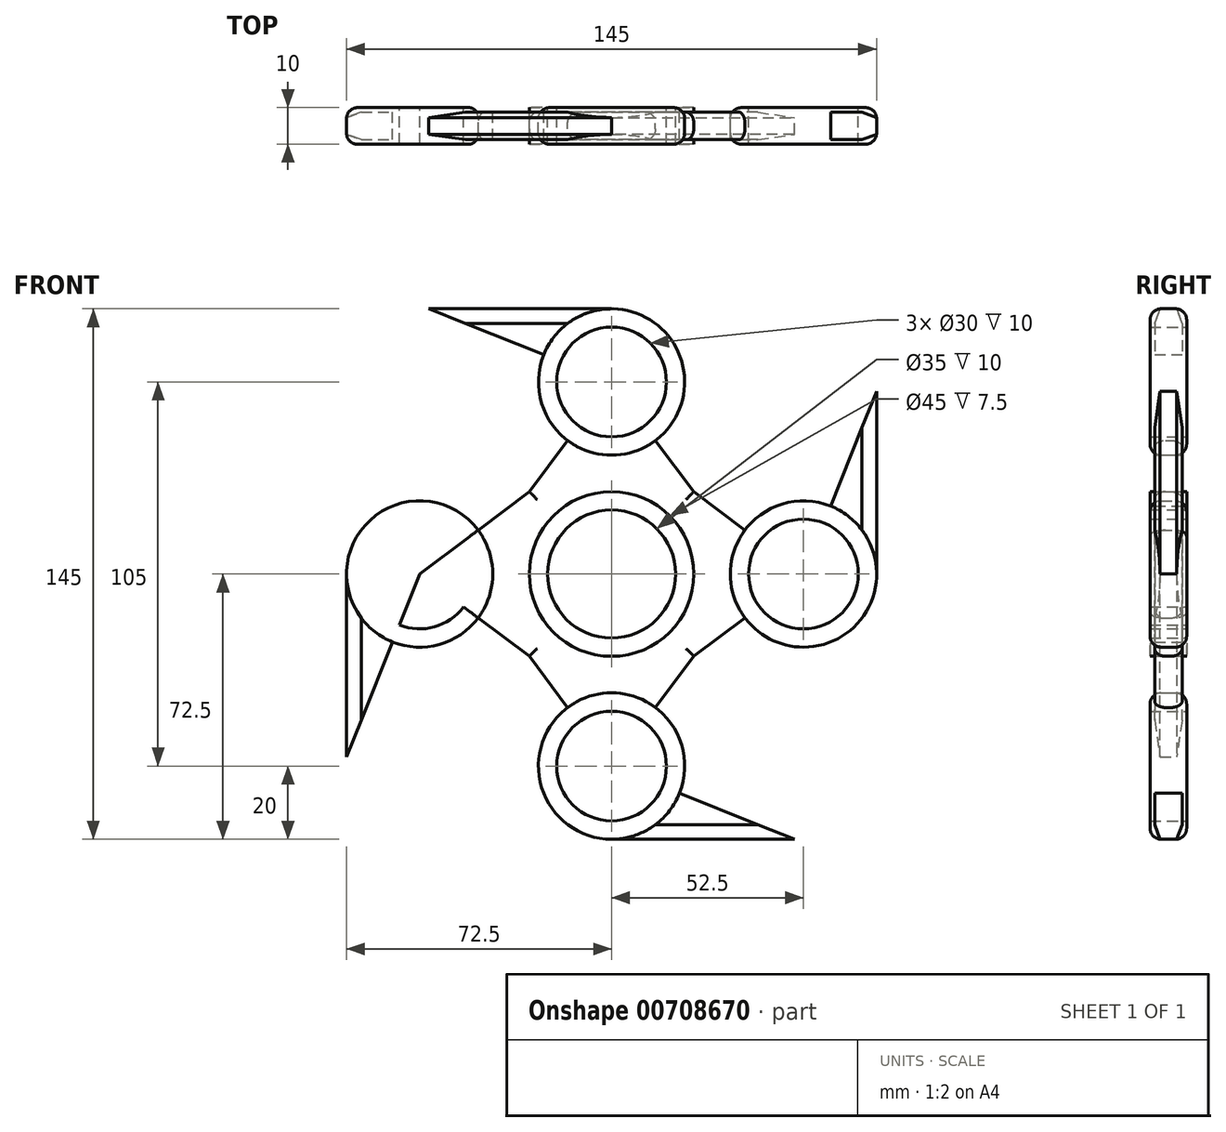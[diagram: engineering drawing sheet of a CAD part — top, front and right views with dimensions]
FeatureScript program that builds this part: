
annotation { "Feature Type Name" : "Feature", "Feature Type Description" : "" }
export const myFeature = defineFeature(function(context is Context, id is Id, definition is map)
    precondition{}
    {
        {
            var Q0;
            Q0=qCreatedBy(makeId("Front.planeOp"),FACE);
            var sketch = newSketch(context, id + "F0", { "sketchPlane" : qUnion([Q0])});
            skCircle(sketch, "E0", {"center": v(0, 0) * mm, "radius": 22.5 * mm});
            skLineSegment(sketch, "E1", {"start": v(0, 75.18) * mm, "end": v(0, -75.66) * mm});
            skLineSegment(sketch, "E2", {"start": v(-75.18, 0) * mm, "end": v(75.18, 0) * mm});
            skLineSegment(sketch, "E3.bottom", {"start": v(22.5, -22.5) * mm, "end": v(-22.5, -22.5) * mm});
            skLineSegment(sketch, "E3.top", {"start": v(22.5, 22.5) * mm, "end": v(-22.5, 22.5) * mm});
            skLineSegment(sketch, "E3.left", {"start": v(22.5, -22.5) * mm, "end": v(22.5, 22.5) * mm});
            skLineSegment(sketch, "E3.right", {"start": v(-22.5, -22.5) * mm, "end": v(-22.5, 22.5) * mm});
            skPoint(sketch, "E4", {"position": v(0, 52.5) * mm});
            skPoint(sketch, "E5", {"position": v(52.5, 0) * mm});
            skPoint(sketch, "E6", {"position": v(0, -52.5) * mm});
            skPoint(sketch, "E7", {"position": v(-52.5, 0) * mm});
            skCircle(sketch, "E8", {"center": v(-52.5, 0) * mm, "radius": 20 * mm});
            skCircle(sketch, "E9", {"center": v(0, 52.5) * mm, "radius": 20 * mm});
            skCircle(sketch, "E10", {"center": v(52.5, 0) * mm, "radius": 20 * mm});
            skCircle(sketch, "E11", {"center": v(0, -52.5) * mm, "radius": 20 * mm});
            skLineSegment(sketch, "E12", {"start": v(-22.5, 22.5) * mm, "end": v(0, 52.5) * mm});
            skLineSegment(sketch, "E13", {"start": v(22.5, 22.5) * mm, "end": v(0, 52.5) * mm});
            skLineSegment(sketch, "E14", {"start": v(22.5, 22.5) * mm, "end": v(52.5, 0) * mm});
            skLineSegment(sketch, "E15", {"start": v(22.5, -22.5) * mm, "end": v(52.5, 0) * mm});
            skLineSegment(sketch, "E16", {"start": v(22.5, -22.5) * mm, "end": v(0, -52.5) * mm});
            skLineSegment(sketch, "E17", {"start": v(-22.5, -22.5) * mm, "end": v(0, -52.5) * mm});
            skLineSegment(sketch, "E18", {"start": v(-22.5, -22.5) * mm, "end": v(-52.5, 0) * mm});
            skLineSegment(sketch, "E19", {"start": v(-52.5, 0) * mm, "end": v(-22.5, 22.5) * mm});
            skPoint(sketch, "E20", {"position": v(0, 72.5) * mm});
            skPoint(sketch, "E21", {"position": v(72.5, 0) * mm});
            skPoint(sketch, "E22", {"position": v(0, -72.5) * mm});
            skPoint(sketch, "E23", {"position": v(-72.5, 0) * mm});
            skLineSegment(sketch, "E24", {"start": v(0, 72.5) * mm, "end": v(-50, 72.5) * mm});
            skLineSegment(sketch, "E25", {"start": v(-50, 72.5) * mm, "end": v(0, 52.5) * mm});
            skLineSegment(sketch, "E26", {"start": v(72.5, 0) * mm, "end": v(72.5, 50) * mm});
            skLineSegment(sketch, "E27", {"start": v(72.5, 50) * mm, "end": v(52.5, 0) * mm});
            skLineSegment(sketch, "E28", {"start": v(0, -72.5) * mm, "end": v(50, -72.5) * mm});
            skLineSegment(sketch, "E29", {"start": v(50, -72.5) * mm, "end": v(0, -52.5) * mm});
            skLineSegment(sketch, "E30", {"start": v(-72.5, 0) * mm, "end": v(-72.5, -50) * mm});
            skLineSegment(sketch, "E31", {"start": v(-72.5, -50) * mm, "end": v(-52.5, 0) * mm});
            skCircle(sketch, "E32", {"center": v(0, 52.5) * mm, "radius": 15 * mm});
            skCircle(sketch, "E33", {"center": v(-52.5, 0) * mm, "radius": 15 * mm});
            skCircle(sketch, "E34", {"center": v(52.5, 0) * mm, "radius": 15 * mm});
            skCircle(sketch, "E35", {"center": v(0, -52.5) * mm, "radius": 15 * mm});
            skCircle(sketch, "E36", {"center": v(0, 0) * mm, "radius": 17.5 * mm});
            skSolve(sketch);
        }
        {
            var Q0;
            {var subQ0=sQuery(id+"F0.wireOp",EDGE,"E24");Q0=makeQuery(id+"F0.imprint","IMPRINT",FACE,{"disambiguationData":[TD([[makeQuery(id+"F0.imprint","IMPRINT",EDGE,{"derivedFrom":subQ0}),1.0]])]});}
            var Q1;
            {var subQ0=sQuery(id+"F0.wireOp",EDGE,"E26");Q1=makeQuery(id+"F0.imprint","IMPRINT",FACE,{"disambiguationData":[TD([[makeQuery(id+"F0.imprint","IMPRINT",EDGE,{"derivedFrom":subQ0}),1.0]])]});}
            var Q2;
            {var subQ0=sQuery(id+"F0.wireOp",EDGE,"E28");Q2=makeQuery(id+"F0.imprint","IMPRINT",FACE,{"disambiguationData":[TD([[makeQuery(id+"F0.imprint","IMPRINT",EDGE,{"derivedFrom":subQ0}),1.0]])]});}
            var Q3;
            {var subQ0=sQuery(id+"F0.wireOp",EDGE,"E30");Q3=makeQuery(id+"F0.imprint","IMPRINT",FACE,{"disambiguationData":[TD([[makeQuery(id+"F0.imprint","IMPRINT",EDGE,{"derivedFrom":subQ0}),1.0]])]});}
            var Q4;
            {var subQ0=sQuery(id+"F0.wireOp",EDGE,"E8");var subQ5=sQuery(id+"F0.wireOp",EDGE,"E18");var subQ6=makeQuery(id+"F0.imprint","INTERSECT",VERTEX,{"derivedFrom":[subQ0,subQ5]});Q4=makeQuery(id+"F0.imprint","IMPRINT",FACE,{"disambiguationData":[TD([[makeQuery(id+"F0.imprint","IMPRINT",EDGE,{"disambiguationData":[TD([[subQ6,-1.0]])],"derivedFrom":subQ0}),-1.0]])]});}
            var Q5;
            {var subQ0=sQuery(id+"F0.wireOp",EDGE,"E8");var subQ5=sQuery(id+"F0.wireOp",EDGE,"E19");var subQ7=makeQuery(id+"F0.imprint","INTERSECT",VERTEX,{"derivedFrom":[subQ0,subQ5]});Q5=makeQuery(id+"F0.imprint","IMPRINT",FACE,{"disambiguationData":[TD([[makeQuery(id+"F0.imprint","IMPRINT",EDGE,{"disambiguationData":[TD([[subQ7,1.0]])],"derivedFrom":subQ0}),-1.0]])]});}
            var Q6;
            {var subQ0=sQuery(id+"F0.wireOp",EDGE,"E9");var subQ5=sQuery(id+"F0.wireOp",EDGE,"E12");var subQ6=makeQuery(id+"F0.imprint","INTERSECT",VERTEX,{"derivedFrom":[subQ0,subQ5]});Q6=makeQuery(id+"F0.imprint","IMPRINT",FACE,{"disambiguationData":[TD([[makeQuery(id+"F0.imprint","IMPRINT",EDGE,{"disambiguationData":[TD([[subQ6,-1.0]])],"derivedFrom":subQ0}),-1.0]])]});}
            var Q7;
            {var subQ0=sQuery(id+"F0.wireOp",EDGE,"E9");var subQ5=sQuery(id+"F0.wireOp",EDGE,"E13");var subQ7=makeQuery(id+"F0.imprint","INTERSECT",VERTEX,{"derivedFrom":[subQ0,subQ5]});Q7=makeQuery(id+"F0.imprint","IMPRINT",FACE,{"disambiguationData":[TD([[makeQuery(id+"F0.imprint","IMPRINT",EDGE,{"disambiguationData":[TD([[subQ7,1.0]])],"derivedFrom":subQ0}),-1.0]])]});}
            var Q8;
            {var subQ0=sQuery(id+"F0.wireOp",EDGE,"E10");var subQ5=sQuery(id+"F0.wireOp",EDGE,"E14");var subQ7=makeQuery(id+"F0.imprint","INTERSECT",VERTEX,{"derivedFrom":[subQ0,subQ5]});Q8=makeQuery(id+"F0.imprint","IMPRINT",FACE,{"disambiguationData":[TD([[makeQuery(id+"F0.imprint","IMPRINT",EDGE,{"disambiguationData":[TD([[subQ7,-1.0]])],"derivedFrom":subQ0}),-1.0]])]});}
            var Q9;
            {var subQ0=sQuery(id+"F0.wireOp",EDGE,"E10");var subQ5=sQuery(id+"F0.wireOp",EDGE,"E15");var subQ7=makeQuery(id+"F0.imprint","INTERSECT",VERTEX,{"derivedFrom":[subQ0,subQ5]});Q9=makeQuery(id+"F0.imprint","IMPRINT",FACE,{"disambiguationData":[TD([[makeQuery(id+"F0.imprint","IMPRINT",EDGE,{"disambiguationData":[TD([[subQ7,1.0]])],"derivedFrom":subQ0}),-1.0]])]});}
            var Q10;
            {var subQ0=sQuery(id+"F0.wireOp",EDGE,"E11");var subQ5=sQuery(id+"F0.wireOp",EDGE,"E16");var subQ6=makeQuery(id+"F0.imprint","INTERSECT",VERTEX,{"derivedFrom":[subQ0,subQ5]});Q10=makeQuery(id+"F0.imprint","IMPRINT",FACE,{"disambiguationData":[TD([[makeQuery(id+"F0.imprint","IMPRINT",EDGE,{"disambiguationData":[TD([[subQ6,-1.0]])],"derivedFrom":subQ0}),-1.0]])]});}
            var Q11;
            {var subQ0=sQuery(id+"F0.wireOp",EDGE,"E11");var subQ5=sQuery(id+"F0.wireOp",EDGE,"E17");var subQ7=makeQuery(id+"F0.imprint","INTERSECT",VERTEX,{"derivedFrom":[subQ0,subQ5]});Q11=makeQuery(id+"F0.imprint","IMPRINT",FACE,{"disambiguationData":[TD([[makeQuery(id+"F0.imprint","IMPRINT",EDGE,{"disambiguationData":[TD([[subQ7,1.0]])],"derivedFrom":subQ0}),-1.0]])]});}
            var Q12;
            {var subQ0=sQuery(id+"F0.wireOp",EDGE,"E3.right");var subQ1=sQuery(id+"F0.wireOp",EDGE,"E0");var subQ2=makeQuery(id+"F0.imprint","INTERSECT",VERTEX,{"derivedFrom":[subQ1,sQuery(id+"F0.wireOp",EDGE,"E2"),subQ0]});Q12=makeQuery(id+"F0.imprint","IMPRINT",FACE,{"disambiguationData":[TD([[makeQuery(id+"F0.imprint","IMPRINT",EDGE,{"disambiguationData":[TD([[subQ2,-1.0]])],"derivedFrom":subQ1}),-1.0]])]});}
            var Q13;
            {var subQ0=sQuery(id+"F0.wireOp",EDGE,"E3.top");var subQ1=sQuery(id+"F0.wireOp",EDGE,"E0");var subQ2=makeQuery(id+"F0.imprint","INTERSECT",VERTEX,{"derivedFrom":[subQ1,sQuery(id+"F0.wireOp",EDGE,"E1"),subQ0]});Q13=makeQuery(id+"F0.imprint","IMPRINT",FACE,{"disambiguationData":[TD([[makeQuery(id+"F0.imprint","IMPRINT",EDGE,{"disambiguationData":[TD([[subQ2,-1.0]])],"derivedFrom":subQ1}),-1.0]])]});}
            var Q14;
            {var subQ0=sQuery(id+"F0.wireOp",EDGE,"E3.top");var subQ1=sQuery(id+"F0.wireOp",EDGE,"E0");var subQ2=makeQuery(id+"F0.imprint","INTERSECT",VERTEX,{"derivedFrom":[subQ1,sQuery(id+"F0.wireOp",EDGE,"E1"),subQ0]});Q14=makeQuery(id+"F0.imprint","IMPRINT",FACE,{"disambiguationData":[TD([[makeQuery(id+"F0.imprint","IMPRINT",EDGE,{"disambiguationData":[TD([[subQ2,1.0]])],"derivedFrom":subQ1}),-1.0]])]});}
            var Q15;
            {var subQ0=sQuery(id+"F0.wireOp",EDGE,"E3.left");var subQ1=sQuery(id+"F0.wireOp",EDGE,"E0");var subQ2=makeQuery(id+"F0.imprint","INTERSECT",VERTEX,{"derivedFrom":[subQ1,sQuery(id+"F0.wireOp",EDGE,"E2"),subQ0]});Q15=makeQuery(id+"F0.imprint","IMPRINT",FACE,{"disambiguationData":[TD([[makeQuery(id+"F0.imprint","IMPRINT",EDGE,{"disambiguationData":[TD([[subQ2,1.0]])],"derivedFrom":subQ1}),-1.0]])]});}
            extrude(context, id + "F1", {"entities" : qUnion([Q0, Q1, Q2, Q3, Q4, Q5, Q6, Q7, Q8, Q9, Q10, Q11, Q12, Q13, Q14, Q15]), "endBound" : BoundingType.SYMMETRIC, "depth" : 7.5 * mm, "offsetDistance" : 25 * mm});
        }
        {
            var Q0;
            {var subQ0=sQuery(id+"F0.wireOp",EDGE,"E8");var subQ5=sQuery(id+"F0.wireOp",EDGE,"E19");var subQ6=makeQuery(id+"F0.imprint","INTERSECT",VERTEX,{"derivedFrom":[subQ0,subQ5]});Q0=makeQuery(id+"F0.imprint","IMPRINT",FACE,{"disambiguationData":[TD([[makeQuery(id+"F0.imprint","IMPRINT",EDGE,{"disambiguationData":[TD([[subQ6,1.0]])],"derivedFrom":subQ5}),1.0]])]});}
            var Q1;
            {var subQ0=sQuery(id+"F0.wireOp",EDGE,"E8");var subQ5=sQuery(id+"F0.wireOp",EDGE,"E31");var subQ6=makeQuery(id+"F0.imprint","INTERSECT",VERTEX,{"derivedFrom":[subQ0,subQ5]});Q1=makeQuery(id+"F0.imprint","IMPRINT",FACE,{"disambiguationData":[TD([[makeQuery(id+"F0.imprint","IMPRINT",EDGE,{"disambiguationData":[TD([[subQ6,-1.0]])],"derivedFrom":subQ5}),1.0]])]});}
            var Q2;
            {var subQ0=sQuery(id+"F0.wireOp",EDGE,"E31");var subQ1=sQuery(id+"F0.wireOp",EDGE,"E8");var subQ2=makeQuery(id+"F0.imprint","INTERSECT",VERTEX,{"derivedFrom":[subQ1,subQ0]});Q2=makeQuery(id+"F0.imprint","IMPRINT",FACE,{"disambiguationData":[TD([[makeQuery(id+"F0.imprint","IMPRINT",EDGE,{"disambiguationData":[TD([[subQ2,-1.0]])],"derivedFrom":subQ1}),1.0]])]});}
            var Q3;
            {var subQ0=sQuery(id+"F0.wireOp",EDGE,"E33");var subQ1=sQuery(id+"F0.wireOp",EDGE,"E2");var subQ2=makeQuery(id+"F0.imprint","INTERSECT",VERTEX,{"disambiguationData":[OD(1.0)],"derivedFrom":[subQ1,subQ0]});Q3=makeQuery(id+"F0.imprint","IMPRINT",FACE,{"disambiguationData":[TD([[makeQuery(id+"F0.imprint","IMPRINT",EDGE,{"disambiguationData":[TD([[subQ2,-1.0]])],"derivedFrom":subQ1}),-1.0]])]});}
            var Q4;
            {var subQ0=sQuery(id+"F0.wireOp",EDGE,"E33");var subQ1=sQuery(id+"F0.wireOp",EDGE,"E2");var subQ2=makeQuery(id+"F0.imprint","INTERSECT",VERTEX,{"disambiguationData":[OD(1.0)],"derivedFrom":[subQ1,subQ0]});Q4=makeQuery(id+"F0.imprint","IMPRINT",FACE,{"disambiguationData":[TD([[makeQuery(id+"F0.imprint","IMPRINT",EDGE,{"disambiguationData":[TD([[subQ2,-1.0]])],"derivedFrom":subQ1}),1.0]])]});}
            var Q5;
            {var subQ0=sQuery(id+"F0.wireOp",EDGE,"E25");var subQ1=sQuery(id+"F0.wireOp",EDGE,"E9");var subQ2=makeQuery(id+"F0.imprint","INTERSECT",VERTEX,{"derivedFrom":[subQ1,subQ0]});Q5=makeQuery(id+"F0.imprint","IMPRINT",FACE,{"disambiguationData":[TD([[makeQuery(id+"F0.imprint","IMPRINT",EDGE,{"disambiguationData":[TD([[subQ2,-1.0]])],"derivedFrom":subQ1}),1.0]])]});}
            var Q6;
            {var subQ0=sQuery(id+"F0.wireOp",EDGE,"E9");var subQ5=sQuery(id+"F0.wireOp",EDGE,"E25");var subQ6=makeQuery(id+"F0.imprint","INTERSECT",VERTEX,{"derivedFrom":[subQ0,subQ5]});Q6=makeQuery(id+"F0.imprint","IMPRINT",FACE,{"disambiguationData":[TD([[makeQuery(id+"F0.imprint","IMPRINT",EDGE,{"disambiguationData":[TD([[subQ6,-1.0]])],"derivedFrom":subQ5}),1.0]])]});}
            var Q7;
            {var subQ0=sQuery(id+"F0.wireOp",EDGE,"E9");var subQ5=sQuery(id+"F0.wireOp",EDGE,"E13");var subQ6=makeQuery(id+"F0.imprint","INTERSECT",VERTEX,{"derivedFrom":[subQ0,subQ5]});Q7=makeQuery(id+"F0.imprint","IMPRINT",FACE,{"disambiguationData":[TD([[makeQuery(id+"F0.imprint","IMPRINT",EDGE,{"disambiguationData":[TD([[subQ6,-1.0]])],"derivedFrom":subQ5}),-1.0]])]});}
            var Q8;
            {var subQ0=sQuery(id+"F0.wireOp",EDGE,"E32");var subQ1=sQuery(id+"F0.wireOp",EDGE,"E1");var subQ2=makeQuery(id+"F0.imprint","INTERSECT",VERTEX,{"disambiguationData":[OD(1.0)],"derivedFrom":[subQ1,subQ0]});Q8=makeQuery(id+"F0.imprint","IMPRINT",FACE,{"disambiguationData":[TD([[makeQuery(id+"F0.imprint","IMPRINT",EDGE,{"disambiguationData":[TD([[subQ2,-1.0]])],"derivedFrom":subQ1}),1.0]])]});}
            var Q9;
            {var subQ0=sQuery(id+"F0.wireOp",EDGE,"E32");var subQ1=sQuery(id+"F0.wireOp",EDGE,"E1");var subQ2=makeQuery(id+"F0.imprint","INTERSECT",VERTEX,{"disambiguationData":[OD(1.0)],"derivedFrom":[subQ1,subQ0]});Q9=makeQuery(id+"F0.imprint","IMPRINT",FACE,{"disambiguationData":[TD([[makeQuery(id+"F0.imprint","IMPRINT",EDGE,{"disambiguationData":[TD([[subQ2,-1.0]])],"derivedFrom":subQ1}),-1.0]])]});}
            var Q10;
            {var subQ0=sQuery(id+"F0.wireOp",EDGE,"E27");var subQ1=sQuery(id+"F0.wireOp",EDGE,"E10");var subQ2=makeQuery(id+"F0.imprint","INTERSECT",VERTEX,{"derivedFrom":[subQ1,subQ0]});Q10=makeQuery(id+"F0.imprint","IMPRINT",FACE,{"disambiguationData":[TD([[makeQuery(id+"F0.imprint","IMPRINT",EDGE,{"disambiguationData":[TD([[subQ2,-1.0]])],"derivedFrom":subQ1}),1.0]])]});}
            var Q11;
            {var subQ0=sQuery(id+"F0.wireOp",EDGE,"E10");var subQ5=sQuery(id+"F0.wireOp",EDGE,"E27");var subQ6=makeQuery(id+"F0.imprint","INTERSECT",VERTEX,{"derivedFrom":[subQ0,subQ5]});Q11=makeQuery(id+"F0.imprint","IMPRINT",FACE,{"disambiguationData":[TD([[makeQuery(id+"F0.imprint","IMPRINT",EDGE,{"disambiguationData":[TD([[subQ6,-1.0]])],"derivedFrom":subQ5}),1.0]])]});}
            var Q12;
            {var subQ0=sQuery(id+"F0.wireOp",EDGE,"E10");var subQ5=sQuery(id+"F0.wireOp",EDGE,"E15");var subQ6=makeQuery(id+"F0.imprint","INTERSECT",VERTEX,{"derivedFrom":[subQ0,subQ5]});Q12=makeQuery(id+"F0.imprint","IMPRINT",FACE,{"disambiguationData":[TD([[makeQuery(id+"F0.imprint","IMPRINT",EDGE,{"disambiguationData":[TD([[subQ6,-1.0]])],"derivedFrom":subQ5}),-1.0]])]});}
            var Q13;
            {var subQ0=sQuery(id+"F0.wireOp",EDGE,"E10");var subQ1=sQuery(id+"F0.wireOp",EDGE,"E2");var subQ2=makeQuery(id+"F0.imprint","INTERSECT",VERTEX,{"derivedFrom":[subQ1,subQ0]});Q13=makeQuery(id+"F0.imprint","IMPRINT",FACE,{"disambiguationData":[TD([[makeQuery(id+"F0.imprint","IMPRINT",EDGE,{"disambiguationData":[TD([[subQ2,-1.0]])],"derivedFrom":subQ1}),-1.0]])]});}
            var Q14;
            {var subQ0=sQuery(id+"F0.wireOp",EDGE,"E10");var subQ1=sQuery(id+"F0.wireOp",EDGE,"E2");var subQ2=makeQuery(id+"F0.imprint","INTERSECT",VERTEX,{"derivedFrom":[subQ1,subQ0]});Q14=makeQuery(id+"F0.imprint","IMPRINT",FACE,{"disambiguationData":[TD([[makeQuery(id+"F0.imprint","IMPRINT",EDGE,{"disambiguationData":[TD([[subQ2,-1.0]])],"derivedFrom":subQ1}),1.0]])]});}
            var Q15;
            {var subQ0=sQuery(id+"F0.wireOp",EDGE,"E11");var subQ1=sQuery(id+"F0.wireOp",EDGE,"E1");var subQ2=makeQuery(id+"F0.imprint","INTERSECT",VERTEX,{"derivedFrom":[subQ1,subQ0]});Q15=makeQuery(id+"F0.imprint","IMPRINT",FACE,{"disambiguationData":[TD([[makeQuery(id+"F0.imprint","IMPRINT",EDGE,{"disambiguationData":[TD([[subQ2,-1.0]])],"derivedFrom":subQ1}),1.0]])]});}
            var Q16;
            {var subQ0=sQuery(id+"F0.wireOp",EDGE,"E16");var subQ1=sQuery(id+"F0.wireOp",EDGE,"E11");var subQ2=makeQuery(id+"F0.imprint","INTERSECT",VERTEX,{"derivedFrom":[subQ1,subQ0]});Q16=makeQuery(id+"F0.imprint","IMPRINT",FACE,{"disambiguationData":[TD([[makeQuery(id+"F0.imprint","IMPRINT",EDGE,{"disambiguationData":[TD([[subQ2,1.0]])],"derivedFrom":subQ1}),1.0]])]});}
            var Q17;
            {var subQ0=sQuery(id+"F0.wireOp",EDGE,"E11");var subQ5=sQuery(id+"F0.wireOp",EDGE,"E29");var subQ6=makeQuery(id+"F0.imprint","INTERSECT",VERTEX,{"derivedFrom":[subQ0,subQ5]});Q17=makeQuery(id+"F0.imprint","IMPRINT",FACE,{"disambiguationData":[TD([[makeQuery(id+"F0.imprint","IMPRINT",EDGE,{"disambiguationData":[TD([[subQ6,-1.0]])],"derivedFrom":subQ5}),1.0]])]});}
            var Q18;
            {var subQ0=sQuery(id+"F0.wireOp",EDGE,"E11");var subQ5=sQuery(id+"F0.wireOp",EDGE,"E17");var subQ6=makeQuery(id+"F0.imprint","INTERSECT",VERTEX,{"derivedFrom":[subQ0,subQ5]});Q18=makeQuery(id+"F0.imprint","IMPRINT",FACE,{"disambiguationData":[TD([[makeQuery(id+"F0.imprint","IMPRINT",EDGE,{"disambiguationData":[TD([[subQ6,-1.0]])],"derivedFrom":subQ5}),-1.0]])]});}
            var Q19;
            {var subQ0=sQuery(id+"F0.wireOp",EDGE,"E11");var subQ1=sQuery(id+"F0.wireOp",EDGE,"E1");var subQ2=makeQuery(id+"F0.imprint","INTERSECT",VERTEX,{"derivedFrom":[subQ1,subQ0]});Q19=makeQuery(id+"F0.imprint","IMPRINT",FACE,{"disambiguationData":[TD([[makeQuery(id+"F0.imprint","IMPRINT",EDGE,{"disambiguationData":[TD([[subQ2,-1.0]])],"derivedFrom":subQ1}),-1.0]])]});}
            var Q20;
            {var subQ3=sQuery(id+"F0.wireOp",EDGE,"E1");var subQ5=sQuery(id+"F0.wireOp",EDGE,"E36");var subQ6=makeQuery(id+"F0.imprint","INTERSECT",VERTEX,{"disambiguationData":[OD(1.0)],"derivedFrom":[subQ3,subQ5]});Q20=makeQuery(id+"F0.imprint","IMPRINT",FACE,{"disambiguationData":[TD([[makeQuery(id+"F0.imprint","IMPRINT",EDGE,{"disambiguationData":[TD([[subQ6,1.0]])],"derivedFrom":subQ5}),-1.0]])]});}
            var Q21;
            {var subQ3=sQuery(id+"F0.wireOp",EDGE,"E1");var subQ5=sQuery(id+"F0.wireOp",EDGE,"E36");var subQ6=makeQuery(id+"F0.imprint","INTERSECT",VERTEX,{"disambiguationData":[OD(1.0)],"derivedFrom":[subQ3,subQ5]});Q21=makeQuery(id+"F0.imprint","IMPRINT",FACE,{"disambiguationData":[TD([[makeQuery(id+"F0.imprint","IMPRINT",EDGE,{"disambiguationData":[TD([[subQ6,-1.0]])],"derivedFrom":subQ5}),-1.0]])]});}
            var Q22;
            {var subQ0=sQuery(id+"F0.wireOp",EDGE,"E1");var subQ5=sQuery(id+"F0.wireOp",EDGE,"E36");var subQ6=makeQuery(id+"F0.imprint","INTERSECT",VERTEX,{"disambiguationData":[OD(0.0)],"derivedFrom":[subQ0,subQ5]});Q22=makeQuery(id+"F0.imprint","IMPRINT",FACE,{"disambiguationData":[TD([[makeQuery(id+"F0.imprint","IMPRINT",EDGE,{"disambiguationData":[TD([[subQ6,1.0]])],"derivedFrom":subQ5}),-1.0]])]});}
            var Q23;
            {var subQ0=sQuery(id+"F0.wireOp",EDGE,"E1");var subQ5=sQuery(id+"F0.wireOp",EDGE,"E36");var subQ6=makeQuery(id+"F0.imprint","INTERSECT",VERTEX,{"disambiguationData":[OD(0.0)],"derivedFrom":[subQ0,subQ5]});Q23=makeQuery(id+"F0.imprint","IMPRINT",FACE,{"disambiguationData":[TD([[makeQuery(id+"F0.imprint","IMPRINT",EDGE,{"disambiguationData":[TD([[subQ6,-1.0]])],"derivedFrom":subQ5}),-1.0]])]});}
            extrude(context, id + "F2", {"entities" : qUnion([Q0, Q1, Q2, Q3, Q4, Q5, Q6, Q7, Q8, Q9, Q10, Q11, Q12, Q13, Q14, Q15, Q16, Q17, Q18, Q19, Q20, Q21, Q22, Q23]), "endBound" : BoundingType.SYMMETRIC, "depth" : 10 * mm, "offsetDistance" : 25 * mm});
        }
        {
            var Q0;
            Q0=makeQuery(id+"F1.opExtrude","CAP_EDGE",EDGE,{"disambiguationData":[OSD([sQuery(id+"F0.wireOp",EDGE,"E24")])],"isStart":false});
            var Q1;
            Q1=makeQuery(id+"F1.opExtrude","CAP_EDGE",EDGE,{"disambiguationData":[OSD([sQuery(id+"F0.wireOp",EDGE,"E26")])],"isStart":false});
            var Q2;
            Q2=makeQuery(id+"F1.opExtrude","CAP_EDGE",EDGE,{"disambiguationData":[OSD([sQuery(id+"F0.wireOp",EDGE,"E28")])],"isStart":false});
            var Q3;
            Q3=makeQuery(id+"F1.opExtrude","CAP_EDGE",EDGE,{"disambiguationData":[OSD([sQuery(id+"F0.wireOp",EDGE,"E30")])],"isStart":false});
            chamfer(context, id + "F3", {"entities" : qUnion([Q0, Q1, Q2, Q3]), "chamferType" : ChamferType.OFFSET_ANGLE, "width" : 4 * mm, "oppositeDirection" : false, "angle" : 20 * degree, "tangentPropagation" : true});
        }
        {
            var Q0;
            Q0=makeQuery(id+"F1.opExtrude","CAP_EDGE",EDGE,{"disambiguationData":[OSD([sQuery(id+"F0.wireOp",EDGE,"E30")])],"isStart":true});
            var Q1;
            Q1=makeQuery(id+"F1.opExtrude","CAP_EDGE",EDGE,{"disambiguationData":[OSD([sQuery(id+"F0.wireOp",EDGE,"E28")])],"isStart":true});
            var Q2;
            Q2=makeQuery(id+"F1.opExtrude","CAP_EDGE",EDGE,{"disambiguationData":[OSD([sQuery(id+"F0.wireOp",EDGE,"E26")])],"isStart":true});
            var Q3;
            Q3=makeQuery(id+"F1.opExtrude","CAP_EDGE",EDGE,{"disambiguationData":[OSD([sQuery(id+"F0.wireOp",EDGE,"E24")])],"isStart":true});
            chamfer(context, id + "F4", {"entities" : qUnion([Q0, Q1, Q2, Q3]), "chamferType" : ChamferType.OFFSET_ANGLE, "width" : 4 * mm, "oppositeDirection" : true, "angle" : 20 * degree, "tangentPropagation" : true});
        }
        {
            var Q0;
            Q0=makeQuery(id+"F1.opExtrude","CAP_EDGE",EDGE,{"disambiguationData":[OSD([sQuery(id+"F0.wireOp",EDGE,"E12")])],"isStart":false});
            var Q1;
            Q1=makeQuery(id+"F1.opExtrude","CAP_EDGE",EDGE,{"disambiguationData":[OSD([sQuery(id+"F0.wireOp",EDGE,"E19")])],"isStart":false});
            var Q2;
            Q2=makeQuery(id+"F1.opExtrude","CAP_EDGE",EDGE,{"disambiguationData":[OSD([sQuery(id+"F0.wireOp",EDGE,"E13")])],"isStart":false});
            var Q3;
            Q3=makeQuery(id+"F1.opExtrude","CAP_EDGE",EDGE,{"disambiguationData":[OSD([sQuery(id+"F0.wireOp",EDGE,"E14")])],"isStart":false});
            var Q4;
            Q4=makeQuery(id+"F1.opExtrude","CAP_EDGE",EDGE,{"disambiguationData":[OSD([sQuery(id+"F0.wireOp",EDGE,"E15")])],"isStart":false});
            var Q5;
            Q5=makeQuery(id+"F1.opExtrude","CAP_EDGE",EDGE,{"disambiguationData":[OSD([sQuery(id+"F0.wireOp",EDGE,"E16")])],"isStart":false});
            var Q6;
            Q6=makeQuery(id+"F1.opExtrude","CAP_EDGE",EDGE,{"disambiguationData":[OSD([sQuery(id+"F0.wireOp",EDGE,"E18")])],"isStart":false});
            var Q7;
            Q7=makeQuery(id+"F1.opExtrude","CAP_EDGE",EDGE,{"disambiguationData":[OSD([sQuery(id+"F0.wireOp",EDGE,"E17")])],"isStart":false});
            var Q8;
            Q8=makeQuery(id+"F1.opExtrude","CAP_EDGE",EDGE,{"disambiguationData":[OSD([sQuery(id+"F0.wireOp",EDGE,"E18")])],"isStart":true});
            var Q9;
            Q9=makeQuery(id+"F1.opExtrude","CAP_EDGE",EDGE,{"disambiguationData":[OSD([sQuery(id+"F0.wireOp",EDGE,"E17")])],"isStart":true});
            var Q10;
            Q10=makeQuery(id+"F1.opExtrude","CAP_EDGE",EDGE,{"disambiguationData":[OSD([sQuery(id+"F0.wireOp",EDGE,"E16")])],"isStart":true});
            var Q11;
            Q11=makeQuery(id+"F1.opExtrude","CAP_EDGE",EDGE,{"disambiguationData":[OSD([sQuery(id+"F0.wireOp",EDGE,"E15")])],"isStart":true});
            var Q12;
            Q12=makeQuery(id+"F1.opExtrude","CAP_EDGE",EDGE,{"disambiguationData":[OSD([sQuery(id+"F0.wireOp",EDGE,"E14")])],"isStart":true});
            var Q13;
            Q13=makeQuery(id+"F1.opExtrude","CAP_EDGE",EDGE,{"disambiguationData":[OSD([sQuery(id+"F0.wireOp",EDGE,"E13")])],"isStart":true});
            var Q14;
            Q14=makeQuery(id+"F1.opExtrude","CAP_EDGE",EDGE,{"disambiguationData":[OSD([sQuery(id+"F0.wireOp",EDGE,"E12")])],"isStart":true});
            var Q15;
            Q15=makeQuery(id+"F1.opExtrude","CAP_EDGE",EDGE,{"disambiguationData":[OSD([sQuery(id+"F0.wireOp",EDGE,"E19")])],"isStart":true});
            fillet(context, id + "F5", {"entities" : qUnion([Q0, Q1, Q2, Q3, Q4, Q5, Q6, Q7, Q8, Q9, Q10, Q11, Q12, Q13, Q14, Q15]), "radius" : 3 * mm, "tangentPropagation" : true, "allowEdgeOverflow" : false});
        }
        {
            var Q0;
            Q0=makeQuery(id+"F2.opExtrude","CAP_EDGE",EDGE,{"disambiguationData":[OSD([sQuery(id+"F0.wireOp",EDGE,"E9")])],"isStart":false});
            var Q1;
            Q1=makeQuery(id+"F2.opExtrude","CAP_EDGE",EDGE,{"disambiguationData":[OSD([sQuery(id+"F0.wireOp",EDGE,"E10")])],"isStart":false});
            var Q2;
            Q2=makeQuery(id+"F2.opExtrude","CAP_EDGE",EDGE,{"disambiguationData":[OSD([sQuery(id+"F0.wireOp",EDGE,"E11")])],"isStart":false});
            var Q3;
            Q3=makeQuery(id+"F2.opExtrude","CAP_EDGE",EDGE,{"disambiguationData":[OSD([sQuery(id+"F0.wireOp",EDGE,"E8")])],"isStart":false});
            fillet(context, id + "F6", {"entities" : qUnion([Q0, Q1, Q2, Q3]), "radius" : 3 * mm, "tangentPropagation" : true, "allowEdgeOverflow" : false});
        }
        {
            var Q0;
            Q0=makeQuery(id+"F2.opExtrude","CAP_EDGE",EDGE,{"disambiguationData":[OSD([sQuery(id+"F0.wireOp",EDGE,"E9")])],"isStart":true});
            var Q1;
            Q1=makeQuery(id+"F2.opExtrude","CAP_EDGE",EDGE,{"disambiguationData":[OSD([sQuery(id+"F0.wireOp",EDGE,"E8")])],"isStart":true});
            var Q2;
            Q2=makeQuery(id+"F2.opExtrude","CAP_EDGE",EDGE,{"disambiguationData":[OSD([sQuery(id+"F0.wireOp",EDGE,"E11")])],"isStart":true});
            var Q3;
            Q3=makeQuery(id+"F2.opExtrude","CAP_EDGE",EDGE,{"disambiguationData":[OSD([sQuery(id+"F0.wireOp",EDGE,"E10")])],"isStart":true});
            fillet(context, id + "F7", {"entities" : qUnion([Q0, Q1, Q2, Q3]), "radius" : 3 * mm, "tangentPropagation" : true, "allowEdgeOverflow" : false});
        }
    });
